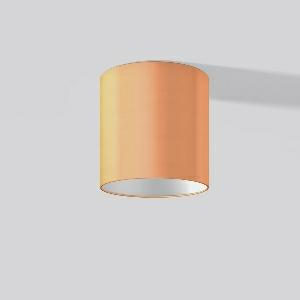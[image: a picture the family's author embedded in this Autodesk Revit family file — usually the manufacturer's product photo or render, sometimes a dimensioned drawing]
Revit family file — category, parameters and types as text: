
# Revit family: toledo_flatliner_901630_002_1_f524
name_source: partatom
category: Lighting Fixtures
units: mm (PartAtom-declared; Revit-internal decimal feet)

## family parameters
Cut with Voids When Loaded = No
Host = Face
Light Source = No
Part Type = Normal
Room Calculation Point = No
Round Connector Dimension = Use Diameter
Shared = No

## types (1)
- 982300.002 (1 x LED Modul 840, 660 lm, 4000)
    Apparent Load = 8 VA
    CIE Flux Codes = 56 78 92 81 100
    Color Rendering = 80
    Color Temperature = 4000
    Default Elevation = 1800 mm
    Description = Series: TOLEDO FLATLINER
Decorative ceiling luminaire for interior decoration. Base luminaire prepared for the installation of fabric lampshade. Cylinder housing sheet steel, powder-coated. Housing: die cast aluminium and sheet steel, powder-coated. Bezel ring: die-cast aluminium, powder-coated. Lightguide and diffuser made of non-yellowing plastic (PMMA) opal matt. Modular design: With the basic luminaire, a square or cylindrical fabric lampshade must always be ordered separately. Fabric lampshades can be fitted to the basic luminaire without tools. Order satin finish diffuser as separate accessory. 
Colour: white
Diameter: 202 mm
Height: 65 mm
Lamp: LED
Socket: without socket
Colour temperature: 4000K
Colour rendering index (CRI): 80
System power: 7.7 W
Rated luminous flux: 660 lm
Luminous efficiency: 86 lm/W
Control gear: Regulated power supply
Protection class: II
Type of protection: IP 40
    Height = 65 mm
    Lamp = 1 x LED Modul 840
    Lamp Light Flux = 660 lm
    Lamp count = 1
    Length = 202 mm
    Lifetime = 50000 h
    Luminous efficacy = 86 lm/W
    Manufacturer = RZB
    ModVariant = No
    Model = 901630.002.1
    Mounting Place = Ceiling
    Mounting Type = Surface mounted
    Number of Poles = 1
    OnlyDefault = Yes
    Power Factor = 1
    Product Name = TOLEDO FLATLINER
    Product group = Surface mounted ceiling Fabric lampshade luminaires
    ProductGroupID = 313
    Protection Class = Protection class II
    Protection Degree = IP 40
    RLX_Detail_Level = 1
    RLX_Emergency_Light_Flux = 0 lm
    RLX_Emergency_Type = 0
    RLX_Emergency_Type_DB = No
    RlxData = <blob elided: 62689 chars, md5=73551c7c>
    Socket = socket
    Standby Power = 0 W
    System Light Flux = 660 lm
    System Power = 8 W
    Type Image = toledo_flatliner_anbau_rund_orange_odeckel.jpg
    URL = http://relux.com
    VarID = 982300_002_5a54
    Voltage = 230 V
    Voltage Range = 220-240 V
    Weight = 0.00 kg
    Width = 0 mm  [stored 0 ft]

note: [stored X ft] marks values corroborated as IEEE doubles in the binary element streams (Revit-internal decimal feet)

## geometry (parser evidence)
native form markers: Blend x4, Sweep x12
no freeform markers — native parametric forms only
